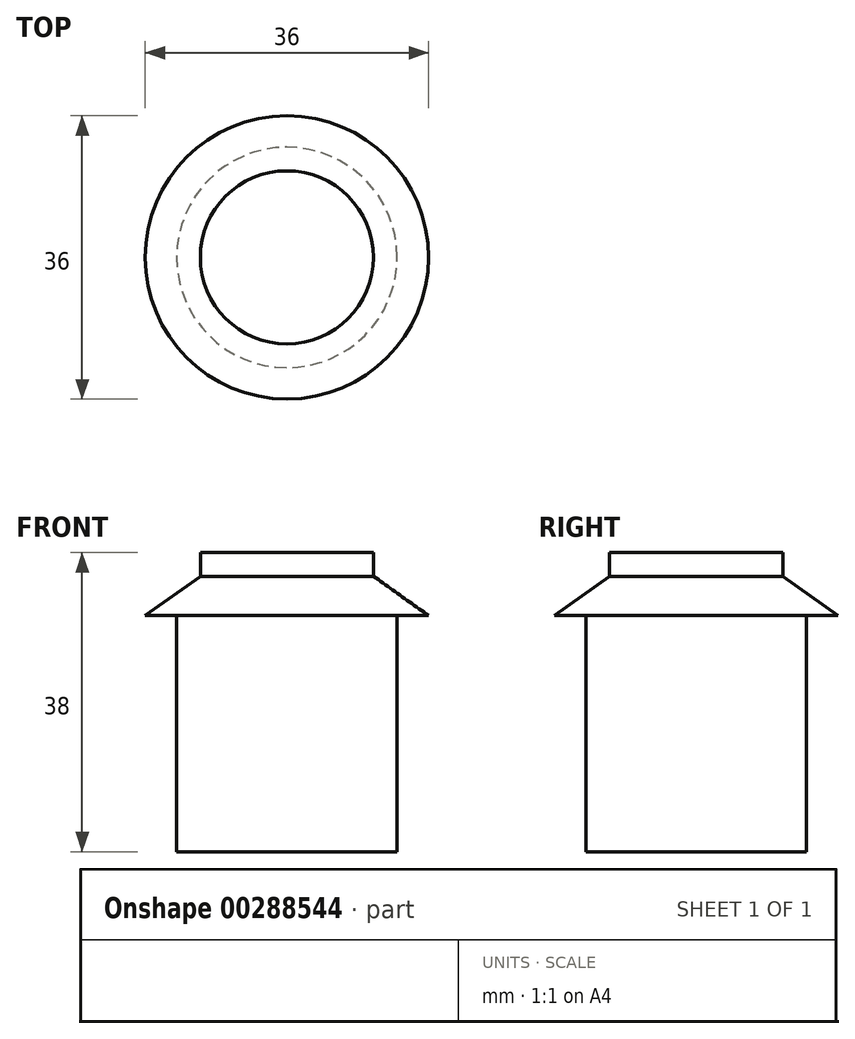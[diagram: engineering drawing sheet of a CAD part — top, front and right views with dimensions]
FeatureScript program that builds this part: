
annotation { "Feature Type Name" : "Feature", "Feature Type Description" : "" }
export const myFeature = defineFeature(function(context is Context, id is Id, definition is map)
    precondition{}
    {
        {
            var Q0;
            Q0=qCreatedBy(makeId("Right.planeOp"),FACE);
            var sketch = newSketch(context, id + "F0", { "sketchPlane" : qUnion([Q0])});
            skLineSegment(sketch, "E0", {"start": v(0, 38) * mm, "end": v(11, 38) * mm});
            skLineSegment(sketch, "E1", {"start": v(11, 38) * mm, "end": v(11, 35) * mm});
            skLineSegment(sketch, "E2", {"start": v(11, 35) * mm, "end": v(18, 30) * mm});
            skLineSegment(sketch, "E3", {"start": v(18, 30) * mm, "end": v(14, 30) * mm});
            skLineSegment(sketch, "E4", {"start": v(14, 30) * mm, "end": v(14, 0) * mm});
            skLineSegment(sketch, "E5", {"start": v(14, 0) * mm, "end": v(0, 0) * mm});
            skLineSegment(sketch, "E6", {"start": v(0, 38) * mm, "end": v(0, 0) * mm});
            skSolve(sketch);
        }
        {
            var Q0;
            Q0=makeQuery(id+"F0.imprint","IMPRINT",FACE,{"disambiguationData":[TD([[makeQuery(id+"F0.imprint","IMPRINT",EDGE,{"derivedFrom":sQuery(id+"F0.wireOp",EDGE,"E0")}),-1.0]])]});
            var Q1;
            Q1=sQuery(id+"F0.wireOp",EDGE,"E6");
            revolve(context, id + "F1", {"entities" : qUnion([Q0]), "axis" : qUnion([Q1]), "revolveType" : RevolveType.FULL});
        }
    });
